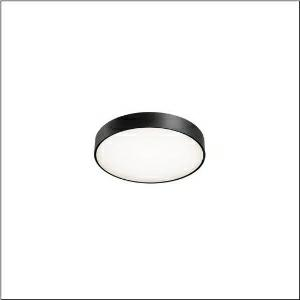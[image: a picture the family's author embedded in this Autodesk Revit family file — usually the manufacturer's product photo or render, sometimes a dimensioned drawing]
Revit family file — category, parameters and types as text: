
# Revit family: round_21_s_51mr34gd0321b
name_source: partatom
category: Lighting Fixtures
units: mm (PartAtom-declared; Revit-internal decimal feet)

## family parameters
Cut with Voids When Loaded = No
Host = Face
Light Source = No
Part Type = Normal
Room Calculation Point = No
Round Connector Dimension = Use Diameter
Shared = No

## types (1)
- Round 21 S (1 x LED, 3930 lm, 28.3 W, 3000K)
    Apparent Load = 28 VA
    CIE Flux Codes = 49 80 96 79 100
    Color Rendering = 80
    Color Temperature = 3000K
    Default Elevation = 1800 mm
    Description = Round 21 S, wall and ceiling luminaire, primary optical cover: cover, of PMMA, opal, light emission: direct/indirect distribution, primary light characteristic: symmetric, installation type: suspended mounting, surface-mounted, LED, rated luminous flux: 3.930lm, luminous efficacy: 139lm/W, light colour: 830, colour temperature: 3000K, control gear: DALI 2, with terminal, 5-pole, mains connection: 230V, AC, 50/60Hz, rated input power: 28.3W, housing, of aluminium, coated, black, diameter: 400mm, height: 62mm, protection rating (complete): IP40, insulation class (complete): insulation class I (protective earthing), certification: CE, impact resistance: IK04, permissible operating ambient temperature: -10..+35°C, packaging unit: 1 piece
    Height = 87 mm
    Lamp = 1 x LED
    Lamp Light Flux = 3930 lm
    Lamp Power = 28.3 W
    Lamp count = 1
    Length = 400 mm
    Luminous efficacy = 139 lm/W
    Manufacturer = Siteco
    ModVariant = No
    Model = 51MR34GD0321B
    Mounting Place = Ceiling
    Mounting Type = Surface mounted
    Number of Poles = 1
    OnlyDefault = Yes
    Power Factor = 1
    Product Name = Round 21 S
    Product group = wall and ceiling luminaire
    ProductGroupID = 304
    Protection Class = Protection class I
    Protection Degree = IP 40
    RLX_Detail_Level = 1
    RLX_Emergency_Light_Flux = 0 lm
    RLX_Emergency_Type = 0
    RLX_Emergency_Type_DB = No
    RlxData = <blob elided: 13865 chars, md5=e99b7fdc>
    Socket = socket
    Standby Power = 0 W
    System Light Flux = 3930 lm
    System Power = 28 W
    Type Comments = Product without accessories
    Type Image = l_1258311.jpg
    URL = http://relux.com
    VarID = ---
    Voltage = 0 V
    Weight = 0.00 kg
    Width = 0 mm  [stored 0 ft]

note: [stored X ft] marks values corroborated as IEEE doubles in the binary element streams (Revit-internal decimal feet)

## geometry (parser evidence)
native form markers: Sweep x15
no freeform markers — native parametric forms only
